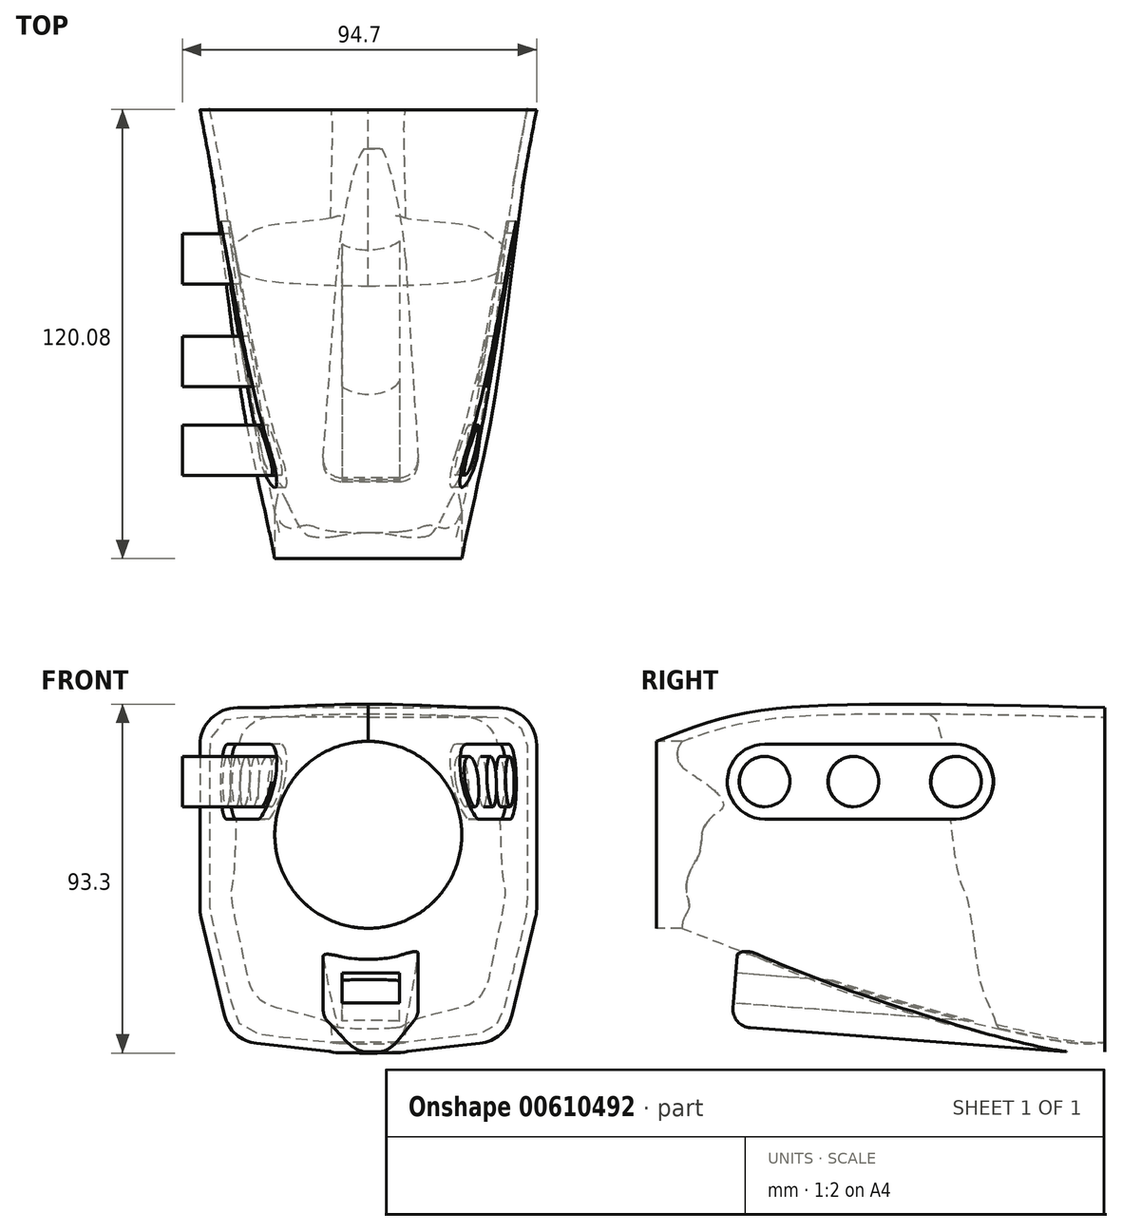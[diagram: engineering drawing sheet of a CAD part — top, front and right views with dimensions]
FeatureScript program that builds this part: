
annotation { "Feature Type Name" : "Feature", "Feature Type Description" : "" }
export const myFeature = defineFeature(function(context is Context, id is Id, definition is map)
    precondition{}
    {
        {
            var Q0;
            Q0=qCreatedBy(makeId("Front.planeOp"),FACE);
            var sketch = newSketch(context, id + "F0", { "sketchPlane" : qUnion([Q0])});
            skLineSegment(sketch, "E0", {"start": v(0, 48) * mm, "end": v(35, 48) * mm});
            skLineSegment(sketch, "E1", {"start": v(45, 38) * mm, "end": v(45, -5.82) * mm});
            skLineSegment(sketch, "E2", {"start": v(44.72, -8.15) * mm, "end": v(38.48, -34.2) * mm});
            skLineSegment(sketch, "E3", {"start": v(29.85, -41.8) * mm, "end": v(10.55, -43.94) * mm});
            skLineSegment(sketch, "E4", {"start": v(9.45, -44) * mm, "end": v(0, -44) * mm});
            skPoint(sketch, "E5.visualSharp", {"position": v(45, 48) * mm});
            skArc(sketch, "E5.filletArc", {"start": v(45, 38) * mm, "mid": v(42.07, 45.07) * mm, "end": v(35, 48) * mm});
            skPoint(sketch, "E6.visualSharp", {"position": v(45, -7) * mm});
            skArc(sketch, "E6.filletArc", {"start": v(44.72, -8.15) * mm, "mid": v(44.93, -7) * mm, "end": v(45, -5.82) * mm});
            skPoint(sketch, "E7.visualSharp", {"position": v(36.84, -41.03) * mm});
            skArc(sketch, "E7.filletArc", {"start": v(29.85, -41.8) * mm, "mid": v(35.37, -39.37) * mm, "end": v(38.48, -34.2) * mm});
            skPoint(sketch, "E8.visualSharp", {"position": v(10, -44) * mm});
            skArc(sketch, "E8.filletArc", {"start": v(9.45, -44) * mm, "mid": v(10, -43.98) * mm, "end": v(10.55, -43.94) * mm});
            skLineSegment(sketch, "E9.MirrorCS", {"start": v(0, 48) * mm, "end": v(-35, 48) * mm});
            skArc(sketch, "E10.MirrorCS", {"start": v(-45, 38) * mm, "mid": v(-42.07, 45.07) * mm, "end": v(-35, 48) * mm});
            skLineSegment(sketch, "E11.MirrorCS", {"start": v(-45, 38) * mm, "end": v(-45, -5.82) * mm});
            skArc(sketch, "E12.MirrorCS", {"start": v(-44.72, -8.15) * mm, "mid": v(-44.93, -7) * mm, "end": v(-45, -5.82) * mm});
            skLineSegment(sketch, "E13.MirrorCS", {"start": v(-44.72, -8.15) * mm, "end": v(-38.48, -34.2) * mm});
            skArc(sketch, "E14.MirrorCS", {"start": v(-29.85, -41.8) * mm, "mid": v(-35.37, -39.37) * mm, "end": v(-38.48, -34.2) * mm});
            skLineSegment(sketch, "E15.MirrorCS", {"start": v(-29.85, -41.8) * mm, "end": v(-10.55, -43.94) * mm});
            skLineSegment(sketch, "E16.MirrorCS", {"start": v(-9.45, -44) * mm, "end": v(0, -44) * mm});
            skArc(sketch, "E17.MirrorCS", {"start": v(-9.45, -44) * mm, "mid": v(-10, -43.98) * mm, "end": v(-10.55, -43.94) * mm});
            skSolve(sketch);
        }
        {
            var Q0;
            Q0=qCreatedBy(makeId("Front.planeOp"),FACE);
            cPlane(context, id + "F1", {"entities" : qUnion([Q0]), "cplaneType" : CPlaneType.OFFSET, "offset" : 120 * mm, "width" : 150 * mm, "height" : 150 * mm});
        }
        {
            var Q0;
            Q0=qCreatedBy(id+"F1.planeOp",FACE);
            var sketch = newSketch(context, id + "F2", { "sketchPlane" : qUnion([Q0])});
            skPoint(sketch, "E18", {"position": v(0, 14) * mm});
            skCircle(sketch, "E19", {"center": v(0, 14) * mm, "radius": 25 * mm});
            skSolve(sketch);
        }
        {
            var Q0;
            Q0=qCreatedBy(makeId("Right.planeOp"),FACE);
            var sketch = newSketch(context, id + "F3", { "sketchPlane" : qUnion([Q0])});
            skLineSegment(sketch, "E20.0", {"start": v(0, -41.8) * mm, "end": v(0, -43.94) * mm});
            skPoint(sketch, "E21.0", {"position": v(0, -44) * mm});
            skPoint(sketch, "E22.0", {"position": v(0, 48) * mm});
            skLineSegment(sketch, "E23.0", {"start": v(-120, -11) * mm, "end": v(-120, 39) * mm});
            skFitSpline(sketch, "E24", {"points": [v(-120, 39) * mm, v(-100.67, 45.56) * mm, v(-72.44, 48.7) * mm, v(0, 48) * mm], "startDerivative": vector(76.76, 29.93) * mm, "endDerivative": vector(173.74, -4.11) * mm});
            skFitSpline(sketch, "E25", {"points": [v(0, -44) * mm, v(-10.35, -44) * mm, v(-69.55, -29.41) * mm, v(-98.49, -19.34) * mm, v(-120, -11) * mm], "startDerivative": vector(-51.13, -6.57) * mm, "endDerivative": vector(-96.5, 37.54) * mm});
            skSolve(sketch);
        }
        {
            var Q0;
            Q0=makeQuery(id+"F2.imprint","IMPRINT",FACE,{"disambiguationData":[TD([[makeQuery(id+"F2.imprint","IMPRINT",EDGE,{"derivedFrom":sQuery(id+"F2.wireOp",EDGE,"E19")}),1.0]])]});
            var Q1;
            Q1=makeQuery(id+"F0.imprint","IMPRINT",FACE,{"disambiguationData":[TD([[makeQuery(id+"F0.imprint","IMPRINT",EDGE,{"derivedFrom":sQuery(id+"F0.wireOp",EDGE,"E0")}),-1.0]])]});
            var Q2;
            Q2=sQuery(id+"F3.wireOp",EDGE,"E24");
            var Q3;
            Q3=sQuery(id+"F3.wireOp",EDGE,"E25");
            loft(context, id + "F4", {"addGuides" : true, "sheetProfilesArray" : [{ "sheetProfileEntities" : qUnion([Q0]) }, { "sheetProfileEntities" : qUnion([Q1]) }], "guidesArray" : [{ "guideEntities" : qUnion([Q2]), "guideDerivativeType" : LoftGuideDerivativeType.DEFAULT, "guideDerivativeMagnitude" : 1 }, { "guideEntities" : qUnion([Q3]), "guideDerivativeType" : LoftGuideDerivativeType.DEFAULT, "guideDerivativeMagnitude" : 1 }]});
        }
        {
            var Q0;
            Q0=makeQuery(id+"F4.opLoft","CAP_FACE",FACE,{"disambiguationData":[OSD([makeQuery(id+"F0.imprint","IMPRINT",FACE,{"disambiguationData":[TD([[makeQuery(id+"F0.imprint","IMPRINT",EDGE,{"derivedFrom":sQuery(id+"F0.wireOp",EDGE,"E0")}),-1.0]])]})])],"isStart":true});
            shell(context, id + "F5", {"entities" : qUnion([Q0]), "thickness" : 2.5 * mm});
        }
        {
            var Q0;
            Q0=makeQuery(id+"F4.opLoft","CAP_FACE",FACE,{"disambiguationData":[OSD([makeQuery(id+"F2.imprint","IMPRINT",FACE,{"disambiguationData":[TD([[makeQuery(id+"F2.imprint","IMPRINT",EDGE,{"derivedFrom":sQuery(id+"F2.wireOp",EDGE,"E19")}),1.0]])]})])],"isStart":true});
            extrude(context, id + "F6", {"entities" : qUnion([Q0]), "operationType" : NewBodyOperationType.REMOVE, "endBound" : BoundingType.THROUGH_ALL, "oppositeDirection" : true, "depth" : 130 * mm, "offsetDistance" : 25 * mm});
        }
        {
            var Q0;
            Q0=qCreatedBy(makeId("Right.planeOp"),FACE);
            var sketch = newSketch(context, id + "F7", { "sketchPlane" : qUnion([Q0])});
            skPoint(sketch, "E26.0", {"position": v(-10.35, -44) * mm});
            skPoint(sketch, "E27.0", {"position": v(-98.49, -19.34) * mm});
            skLineSegment(sketch, "E28", {"start": v(-98.49, -19.34) * mm, "end": v(-98.49, -37.35) * mm});
            skLineSegment(sketch, "E29", {"start": v(-98.49, -37.35) * mm, "end": v(-10.35, -44) * mm});
            skSolve(sketch);
        }
        {
            var Q0;
            Q0=sQuery(id+"F7.wireOp",EDGE,"E29");
            var Q1;
            Q1=sQuery(id+"F7.wireOp",EDGE,"E28");
            cPlane(context, id + "F8", {"entities" : qUnion([Q0, Q1]), "cplaneType" : CPlaneType.LINE_ANGLE, "offset" : 25 * mm, "angle" : 90 * degree, "width" : 150 * mm, "height" : 150 * mm});
        }
        {
            var Q0;
            Q0=qCreatedBy(id+"F8.planeOp",FACE);
            var sketch = newSketch(context, id + "F9", { "sketchPlane" : qUnion([Q0])});
            skPoint(sketch, "E30.0", {"position": v(0, -96.75) * mm});
            skPoint(sketch, "E31.0", {"position": v(0, -7.02) * mm});
            skLineSegment(sketch, "E32", {"start": v(0, -96.75) * mm, "end": v(13.66, -96.75) * mm});
            skLineSegment(sketch, "E33", {"start": v(13.66, -96.75) * mm, "end": v(8.1, -7.02) * mm});
            skLineSegment(sketch, "E34", {"start": v(8.1, -7.02) * mm, "end": v(0, -7.02) * mm});
            skLineSegment(sketch, "E35", {"start": v(-6, -7.02) * mm, "end": v(-12.45, -96.75) * mm});
            skLineSegment(sketch, "E36", {"start": v(-12.45, -96.75) * mm, "end": v(0, -96.75) * mm});
            skLineSegment(sketch, "E37", {"start": v(0, -7.02) * mm, "end": v(-6, -7.02) * mm});
            skSolve(sketch);
        }
        {
            var Q0;
            Q0=makeQuery(id+"F9.imprint","IMPRINT",FACE,{"disambiguationData":[TD([[makeQuery(id+"F9.imprint","IMPRINT",EDGE,{"derivedFrom":sQuery(id+"F9.wireOp",EDGE,"E32")}),1.0]])]});
            var Q1;
            Q1=makeQuery(id+"F4.opLoft","SWEPT_FACE",FACE,{"disambiguationData":[OSD([sQuery(id+"F0.wireOp",EDGE,"E0"),sQuery(id+"F0.wireOp",EDGE,"E5.filletArc"),sQuery(id+"F0.wireOp",EDGE,"E9.MirrorCS"),sQuery(id+"F2.wireOp",EDGE,"E19"),sQuery(id+"F3.wireOp",EDGE,"E24")])]});
            extrude(context, id + "F10", {"entities" : qUnion([Q0]), "operationType" : NewBodyOperationType.ADD, "endBound" : BoundingType.UP_TO_SURFACE, "depth" : 25 * mm, "endBoundEntityFace" : qUnion([Q1]), "offsetDistance" : 25 * mm});
        }
        {
            var Q0;
            Q0=makeQuery(id+"F10.opExtrude","SWEPT_EDGE",EDGE,{"disambiguationData":[OSD([sQuery(id+"F9.wireOp",EDGE,"E32"),sQuery(id+"F9.wireOp",EDGE,"E33")])]});
            var Q1;
            Q1=makeQuery(id+"F10.opExtrude","SWEPT_EDGE",EDGE,{"disambiguationData":[OSD([sQuery(id+"F9.wireOp",EDGE,"E35"),sQuery(id+"F9.wireOp",EDGE,"E36")])]});
            var Q2;
            Q2=makeQuery(id+"F10.opExtrude","CAP_EDGE",EDGE,{"disambiguationData":[OSD([sQuery(id+"F9.wireOp",EDGE,"E33")])],"isStart":true});
            var Q3;
            Q3=makeQuery(id+"F10.opExtrude","CAP_EDGE",EDGE,{"disambiguationData":[OSD([sQuery(id+"F9.wireOp",EDGE,"E35")])],"isStart":true});
            var Q4;
            Q4=makeQuery(id+"F10.opExtrude","CAP_EDGE",EDGE,{"disambiguationData":[OSD([sQuery(id+"F9.wireOp",EDGE,"E32"),sQuery(id+"F9.wireOp",EDGE,"E36")])],"isStart":true});
            fillet(context, id + "F11", {"entities" : qUnion([Q0, Q1, Q2, Q3, Q4]), "radius" : 5 * mm, "tangentPropagation" : true, "allowEdgeOverflow" : false});
        }
        {
            var Q0;
            Q0=makeQuery(id+"F10.opExtrude","SWEPT_FACE",FACE,{"disambiguationData":[OSD([sQuery(id+"F9.wireOp",EDGE,"E32"),sQuery(id+"F9.wireOp",EDGE,"E36")])]});
            var sketch = newSketch(context, id + "F12", { "sketchPlane" : qUnion([Q0])});
            skLineSegment(sketch, "E38", {"start": v(-7.08, -30.38) * mm, "end": v(8.34, -30.38) * mm});
            skLineSegment(sketch, "E39", {"start": v(8.34, -30.38) * mm, "end": v(8.34, -38.4) * mm});
            skLineSegment(sketch, "E40", {"start": v(8.34, -38.4) * mm, "end": v(-7.08, -38.4) * mm});
            skLineSegment(sketch, "E41", {"start": v(-7.08, -38.4) * mm, "end": v(-7.08, -30.38) * mm});
            skSolve(sketch);
        }
        {
            var Q0;
            Q0=makeQuery(id+"F12.imprint","IMPRINT",FACE,{"disambiguationData":[TD([[makeQuery(id+"F12.imprint","IMPRINT",EDGE,{"derivedFrom":sQuery(id+"F12.wireOp",EDGE,"E38")}),-1.0]])]});
            extrude(context, id + "F13", {"entities" : qUnion([Q0]), "operationType" : NewBodyOperationType.REMOVE, "endBound" : BoundingType.THROUGH_ALL, "oppositeDirection" : true, "depth" : 25 * mm, "offsetDistance" : 25 * mm});
        }
        {
            var Q0;
            Q0=qCreatedBy(makeId("Right.planeOp"),FACE);
            cPlane(context, id + "F14", {"entities" : qUnion([Q0]), "cplaneType" : CPlaneType.OFFSET, "offset" : 55 * mm, "width" : 150 * mm, "height" : 150 * mm});
        }
        {
            var Q0;
            Q0=qCreatedBy(id+"F14.planeOp",FACE);
            var sketch = newSketch(context, id + "F15", { "sketchPlane" : qUnion([Q0])});
            skLineSegment(sketch, "E42", {"start": v(-105.47, 28.23) * mm, "end": v(-14.98, 28.23) * mm, "construction": true});
            skCircle(sketch, "E43", {"center": v(-90.96, 28.23) * mm, "radius": 6.73 * mm});
            skCircle(sketch, "E44", {"center": v(-67.22, 28.23) * mm, "radius": 6.73 * mm});
            skCircle(sketch, "E45", {"center": v(-39.78, 28.23) * mm, "radius": 6.73 * mm});
            skSolve(sketch);
        }
        {
            var Q0;
            Q0=sQuery(id+"F15.wireOp",EDGE,"E43");
            var Q1;
            Q1=makeQuery(id+"F4.opLoft","SWEPT_FACE",FACE,{"disambiguationData":[OSD([sQuery(id+"F0.wireOp",EDGE,"E0"),sQuery(id+"F0.wireOp",EDGE,"E5.filletArc"),sQuery(id+"F0.wireOp",EDGE,"E9.MirrorCS"),sQuery(id+"F2.wireOp",EDGE,"E19"),sQuery(id+"F3.wireOp",EDGE,"E24")])]});
            extrude(context, id + "F16", {"bodyType" : ToolBodyType.SURFACE, "surfaceEntities" : qUnion([Q0]), "endBound" : BoundingType.UP_TO_SURFACE, "oppositeDirection" : true, "depth" : 25 * mm, "endBoundEntityFace" : qUnion([Q1]), "offsetDistance" : 25 * mm});
        }
        {
            var Q0;
            Q0=sQuery(id+"F15.wireOp",EDGE,"E44");
            var Q1;
            Q1=sQuery(id+"F15.wireOp",EDGE,"E45");
            var Q2;
            Q2=makeQuery(id+"F4.opLoft","SWEPT_FACE",FACE,{"disambiguationData":[OSD([sQuery(id+"F0.wireOp",EDGE,"E0"),sQuery(id+"F0.wireOp",EDGE,"E5.filletArc"),sQuery(id+"F0.wireOp",EDGE,"E9.MirrorCS"),sQuery(id+"F2.wireOp",EDGE,"E19"),sQuery(id+"F3.wireOp",EDGE,"E24")])]});
            extrude(context, id + "F17", {"bodyType" : ToolBodyType.SURFACE, "surfaceEntities" : qUnion([Q0, Q1]), "endBound" : BoundingType.UP_TO_SURFACE, "oppositeDirection" : true, "depth" : 32.2 * mm, "endBoundEntityFace" : qUnion([Q2]), "offsetDistance" : 25 * mm});
        }
        {
            var Q0;
            Q0=makeQuery(id+"F4.opLoft","CAP_FACE",FACE,{"disambiguationData":[OSD([makeQuery(id+"F0.imprint","IMPRINT",FACE,{"disambiguationData":[TD([[makeQuery(id+"F0.imprint","IMPRINT",EDGE,{"derivedFrom":sQuery(id+"F0.wireOp",EDGE,"E0")}),-1.0]])]})])],"isStart":true});
            var sketch = newSketch(context, id + "F18", { "sketchPlane" : qUnion([Q0])});
            skLineSegment(sketch, "E46", {"start": v(49.74, 36) * mm, "end": v(49.74, -32.48) * mm});
            skSolve(sketch);
        }
        {
            var Q0;
            {var subQ0=sQuery(id+"F9.wireOp",EDGE,"E36");var subQ3=sQuery(id+"F9.wireOp",EDGE,"E32");Q0=makeQuery(id+"F13.boolean.opBoolean","SPLIT",FACE,{"disambiguationData":[TD([makeQuery(id+"F13.opExtrude","SWEPT_FACE",FACE,{"disambiguationData":[OSD([sQuery(id+"F12.wireOp",EDGE,"E38")])]})])],"derivedFrom":makeQuery(id+"F10.opExtrude","SWEPT_FACE",FACE,{"disambiguationData":[OSD([subQ3,subQ0])]})});}
            var sketch = newSketch(context, id + "F19", { "sketchPlane" : qUnion([Q0])});
            skLineSegment(sketch, "E47", {"start": v(-49.64, 25.5) * mm, "end": v(-49.64, -33.43) * mm});
            skSolve(sketch);
        }
        {
            var Q0;
            Q0=sQuery(id+"F18.wireOp",VERTEX,"E46.end");
            var Q1;
            Q1=sQuery(id+"F18.wireOp",VERTEX,"E46.start");
            var Q2;
            Q2=sQuery(id+"F19.wireOp",VERTEX,"E47.start");
            cPlane(context, id + "F20", {"entities" : qUnion([Q0, Q1, Q2]), "cplaneType" : CPlaneType.THREE_POINT, "offset" : 25 * mm, "width" : 150 * mm, "height" : 150 * mm});
        }
        {
            var Q0;
            Q0=qCreatedBy(id+"F20.planeOp",FACE);
            var sketch = newSketch(context, id + "F21", { "sketchPlane" : qUnion([Q0])});
            skPoint(sketch, "E48.0", {"position": v(91.02, 28.23) * mm});
            skPoint(sketch, "E49.0", {"position": v(39.84, 28.23) * mm});
            skPoint(sketch, "E50.0", {"position": v(67.28, 28.23) * mm});
            skArc(sketch, "E51", {"start": v(39.84, 38.23) * mm, "mid": v(29.84, 28.23) * mm, "end": v(39.84, 18.23) * mm});
            skArc(sketch, "E52", {"start": v(91.02, 18.23) * mm, "mid": v(101.02, 28.23) * mm, "end": v(91.02, 38.23) * mm});
            skLineSegment(sketch, "E53", {"start": v(39.84, 38.23) * mm, "end": v(91.02, 38.23) * mm});
            skLineSegment(sketch, "E54", {"start": v(39.84, 18.23) * mm, "end": v(91.02, 18.23) * mm});
            skSolve(sketch);
        }
        {
            var Q0;
            Q0=makeQuery(id+"F21.imprint","IMPRINT",FACE,{"disambiguationData":[TD([[makeQuery(id+"F21.imprint","IMPRINT",EDGE,{"derivedFrom":sQuery(id+"F21.wireOp",EDGE,"E51")}),1.0]])]});
            var Q1;
            Q1=makeQuery(id+"F4.opLoft","SWEPT_FACE",FACE,{"disambiguationData":[OSD([sQuery(id+"F0.wireOp",EDGE,"E0"),sQuery(id+"F0.wireOp",EDGE,"E5.filletArc"),sQuery(id+"F0.wireOp",EDGE,"E9.MirrorCS"),sQuery(id+"F2.wireOp",EDGE,"E19"),sQuery(id+"F3.wireOp",EDGE,"E24")])]});
            extrude(context, id + "F22", {"entities" : qUnion([Q0]), "endBound" : BoundingType.UP_TO_SURFACE, "oppositeDirection" : true, "depth" : 25 * mm, "endBoundEntityFace" : qUnion([Q1]), "offsetDistance" : 25 * mm});
        }
        {
            var Q0;
            Q0=qCreatedBy(id+"F20.planeOp",FACE);
            var sketch = newSketch(context, id + "F23", { "sketchPlane" : qUnion([Q0])});
            skCircle(sketch, "E55.0", {"center": v(39.84, 28.23) * mm, "radius": 6.73 * mm});
            skCircle(sketch, "E56.0", {"center": v(67.28, 28.23) * mm, "radius": 6.73 * mm});
            skLineSegment(sketch, "E57.0.0", {"start": v(39.84, 18.23) * mm, "end": v(91.02, 18.23) * mm});
            skArc(sketch, "E57.0.1", {"start": v(91.02, 18.23) * mm, "mid": v(101.02, 28.23) * mm, "end": v(91.02, 38.23) * mm});
            skLineSegment(sketch, "E57.0.2", {"start": v(91.02, 38.23) * mm, "end": v(39.84, 38.23) * mm});
            skArc(sketch, "E57.0.3", {"start": v(39.84, 38.23) * mm, "mid": v(29.84, 28.23) * mm, "end": v(39.84, 18.23) * mm});
            skCircle(sketch, "E58.0", {"center": v(91.02, 28.23) * mm, "radius": 6.73 * mm});
            skSolve(sketch);
        }
        {
            var Q0;
            Q0=makeQuery(id+"F23.imprint","IMPRINT",FACE,{"disambiguationData":[TD([[makeQuery(id+"F23.imprint","IMPRINT",EDGE,{"derivedFrom":sQuery(id+"F23.wireOp",EDGE,"E55.0")}),-1.0]])]});
            var Q1;
            Q1=makeQuery(id+"F23.imprint","IMPRINT",FACE,{"disambiguationData":[TD([[makeQuery(id+"F23.imprint","IMPRINT",EDGE,{"derivedFrom":sQuery(id+"F23.wireOp",EDGE,"E56.0")}),-1.0]])]});
            var Q2;
            Q2=makeQuery(id+"F23.imprint","IMPRINT",FACE,{"disambiguationData":[TD([[makeQuery(id+"F23.imprint","IMPRINT",EDGE,{"derivedFrom":sQuery(id+"F23.wireOp",EDGE,"E58.0")}),-1.0]])]});
            extrude(context, id + "F24", {"entities" : qUnion([Q0, Q1, Q2]), "operationType" : NewBodyOperationType.REMOVE, "endBound" : BoundingType.THROUGH_ALL, "oppositeDirection" : true, "depth" : 25 * mm, "offsetDistance" : 25 * mm});
        }
    });
